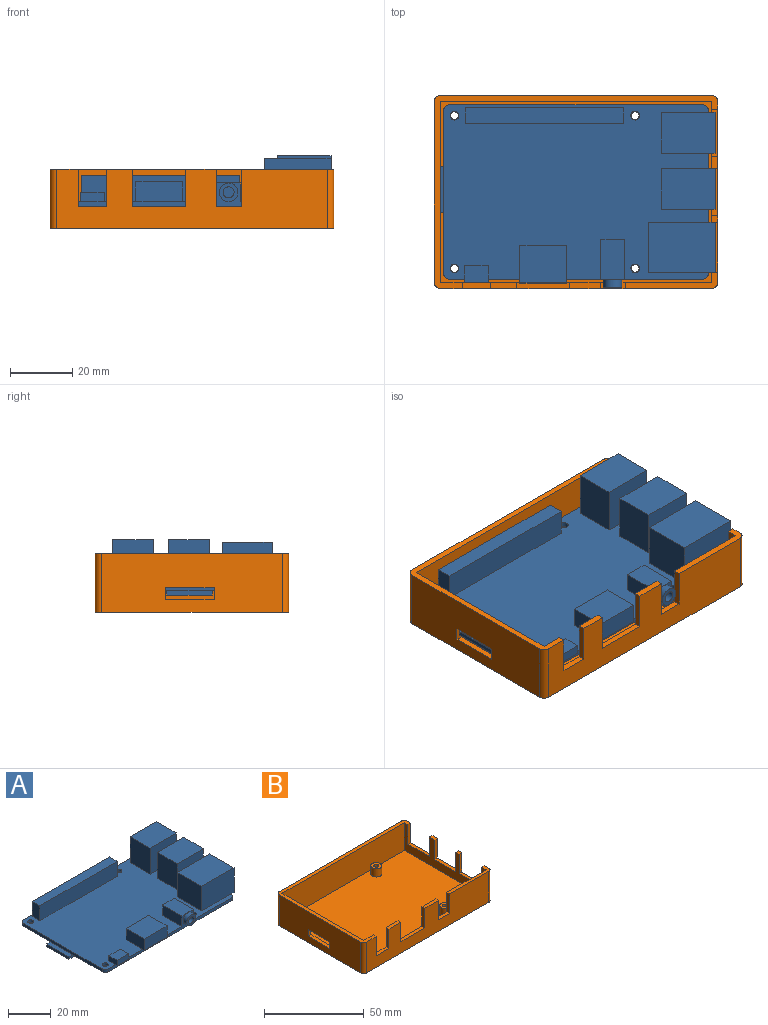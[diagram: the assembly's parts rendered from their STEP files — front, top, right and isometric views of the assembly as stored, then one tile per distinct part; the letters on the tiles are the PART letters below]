
ASSEMBLY  parts=2 mates=1
PART A: 68 faces, bbox 89.5x58.5x18.2 mm
  f0: plane 85x56mm, normal (0,0,1), area 3489.1mm2, adj f1,f2,f3,f4,f5,f6,f7,f8
  f1: plane 81x1.6mm, normal (0,1,0), area 129.6mm2, adj f0,f2,f12,f13
  f2: cylinder r=2mm len=2mm, axis (0,0,-1), area 5mm2, adj f0,f1,f3,f13
  f3: plane 52x1.6mm, normal (-1,0,0), area 83.2mm2, adj f0,f2,f4,f13,f42
  f4: cylinder r=2mm len=2mm, axis (0,0,-1), area 5mm2, adj f0,f3,f5,f13
  f5: plane 81x7.6mm, normal (0,-1,0), area 146.3mm2, adj f0,f4,f6,f13,f48,f54,f60,f62
  f6: cylinder r=2mm len=2mm, axis (0,0,-1), area 5mm2, adj f0,f5,f7,f13
  f7: plane 52x1.6mm, normal (1,0,0), area 83.2mm2, adj f0,f6,f12,f13,f14,f20,f26
  f8: cylinder r=1.4mm len=2.8mm, axis (0,0,-1), area 14.1mm2, adj f0,f13
  f9: cylinder r=1.4mm len=2.8mm, axis (0,0,-1), area 14.1mm2, adj f0,f13
  f10: cylinder r=1.4mm len=2.8mm, axis (0,0,-1), area 14.1mm2, adj f0,f13
  f11: cylinder r=1.4mm len=2.8mm, axis (0,0,-1), area 14.1mm2, adj f0,f13
  f12: cylinder r=2mm len=2mm, axis (0,0,-1), area 5mm2, adj f0,f1,f7,f13
  f13: plane 85x56mm, normal (0,0,-1), area 4264.8mm2, adj f1,f2,f3,f4,f5,f6,f7,f8
  f14: plane 13.1x2.1mm, normal (0,0,-1), area 27.5mm2, adj f7,f15,f16,f17
  f15: plane 17.2x14.8mm, normal (0,-1,0), area 254.6mm2, adj f0,f14,f16,f18,f19
  f16: plane 14.8x13.1mm, normal (1,0,0), area 193.9mm2, adj f14,f15,f17,f19
  f17: plane 17.2x14.8mm, normal (0,1,0), area 254.6mm2, adj f0,f14,f16,f18,f19
  f18: plane 14.8x13.1mm, normal (-1,0,0), area 193.9mm2, adj f0,f15,f17,f19
  f19: plane 17.2x13.1mm, normal (0,0,1), area 225.3mm2, adj f15,f16,f17,f18
  f20: plane 13.1x2.1mm, normal (0,0,-1), area 27.5mm2, adj f7,f21,f22,f23
  f21: plane 17.2x14.8mm, normal (0,-1,0), area 254.6mm2, adj f0,f20,f22,f24,f25
  f22: plane 14.8x13.1mm, normal (1,0,0), area 193.9mm2, adj f20,f21,f23,f25
  f23: plane 17.2x14.8mm, normal (0,1,0), area 254.6mm2, adj f0,f20,f22,f24,f25
  f24: plane 14.8x13.1mm, normal (-1,0,0), area 193.9mm2, adj f0,f21,f23,f25
  f25: plane 17.2x13.1mm, normal (0,0,1), area 225.3mm2, adj f21,f22,f23,f24
  f26: plane 15.9x2.1mm, normal (0,0,-1), area 33.4mm2, adj f7,f27,f28,f29
  f27: plane 21.2x14mm, normal (0,-1,0), area 296.8mm2, adj f0,f26,f28,f30,f31
  f28: plane 15.9x14mm, normal (1,0,0), area 222.6mm2, adj f26,f27,f29,f31
  f29: plane 21.2x14mm, normal (0,1,0), area 296.8mm2, adj f0,f26,f28,f30,f31
  f30: plane 15.9x14mm, normal (-1,0,0), area 222.6mm2, adj f0,f27,f29,f31
  f31: plane 21.2x15.9mm, normal (0,0,1), area 337.1mm2, adj f27,f28,f29,f30
  f32: plane 8.5x5mm, normal (-1,0,0), area 42.5mm2, adj f0,f33,f35,f36
  f33: plane 50.8x8.5mm, normal (0,-1,0), area 431.8mm2, adj f0,f32,f34,f36
  f34: plane 8.5x5mm, normal (1,0,0), area 42.5mm2, adj f0,f33,f35,f36
  f35: plane 50.8x8.5mm, normal (0,1,0), area 431.8mm2, adj f0,f32,f34,f36
  f36: plane 50.8x5mm, normal (0,0,1), area 254mm2, adj f32,f33,f34,f35
  f37: plane 5x1.8mm, normal (-1,0,0), area 9mm2, adj f13,f38,f40,f41
  f38: plane 50.8x1.8mm, normal (0,-1,0), area 91.4mm2, adj f13,f37,f39,f41
  f39: plane 5x1.8mm, normal (1,0,0), area 9mm2, adj f13,f38,f40,f41
  f40: plane 50.8x1.8mm, normal (0,1,0), area 91.4mm2, adj f13,f37,f39,f41
  f41: plane 50.8x5mm, normal (0,0,-1), area 254mm2, adj f37,f38,f39,f40
  f42: plane 14.6x2.4mm, normal (0,0,1), area 35mm2, adj f3,f43,f44,f46
  f43: plane 14.6x1.4mm, normal (-1,0,0), area 20.4mm2, adj f42,f44,f46,f47
  f44: plane 17x1.4mm, normal (0,1,0), area 23.8mm2, adj f13,f42,f43,f45,f47
  f45: plane 14.6x1.4mm, normal (1,0,0), area 20.4mm2, adj f13,f44,f46,f47
  f46: plane 17x1.4mm, normal (0,-1,0), area 23.8mm2, adj f13,f42,f43,f45,f47
  f47: plane 17x14.6mm, normal (0,0,-1), area 248.2mm2, adj f43,f44,f45,f46
  f48: plane 7.5x1mm, normal (0,0,-1), area 7.5mm2, adj f5,f49,f50,f51
  f49: plane 5.4x3mm, normal (-1,0,0), area 16.2mm2, adj f0,f48,f50,f52,f53
  f50: plane 7.5x3mm, normal (0,-1,0), area 22.5mm2, adj f48,f49,f51,f53
  f51: plane 5.4x3mm, normal (1,0,0), area 16.2mm2, adj f0,f48,f50,f52,f53
  f52: plane 7.5x3mm, normal (0,1,0), area 22.5mm2, adj f0,f49,f51,f53
  f53: plane 7.5x5.4mm, normal (0,0,1), area 40.5mm2, adj f49,f50,f51,f52
  f54: plane 15x1.2mm, normal (0,0,-1), area 18mm2, adj f5,f55,f57,f58
  f55: plane 12x6.4mm, normal (1,0,0), area 76.8mm2, adj f0,f54,f56,f58,f59
  f56: plane 15x6.4mm, normal (0,1,0), area 96mm2, adj f0,f55,f57,f59
  f57: plane 12x6.4mm, normal (-1,0,0), area 76.8mm2, adj f0,f54,f56,f58,f59
  f58: plane 15x6.4mm, normal (0,-1,0), area 96mm2, adj f54,f55,f57,f59
  f59: plane 15x12mm, normal (0,0,1), area 180mm2, adj f55,f56,f57,f58
  f60: plane 12.6x6mm, normal (1,0,0), area 75.6mm2, adj f0,f5,f61,f63
  f61: plane 7.5x6mm, normal (0,1,0), area 45mm2, adj f0,f60,f62,f63
  f62: plane 12.6x6mm, normal (-1,0,0), area 75.6mm2, adj f0,f5,f61,f63
  f63: plane 12.6x7.5mm, normal (0,0,1), area 94.5mm2, adj f5,f60,f61,f62
  f64: cylinder r=1.75mm len=3.5mm, axis (0,1,0), area 27.5mm2, adj f66,f67
  f65: cylinder r=3mm len=6mm, axis (0,1,0), area 47.1mm2, adj f5,f66
  f66: plane 6x6mm, normal (0,-1,0), area 18.7mm2, adj f64,f65
  f67: plane 3.5x3.5mm, normal (0,-1,0), area 9.6mm2, adj f64
PART B: 54 faces, bbox 91x62x19 mm
  f0: plane 58x19mm, normal (-1,0,0), area 1039.6mm2, adj f8,f12,f46,f47,f50,f51,f52,f53
  f1: plane 58x17mm, normal (1,0,0), area 923.6mm2, adj f4,f8,f14,f15,f50,f51,f52,f53
  f2: plane 87x19mm, normal (0,-1,0), area 1245mm2, adj f5,f8,f9,f10,f12,f28,f29,f30
  f3: plane 58x19mm, normal (1,0,0), area 548.8mm2, adj f6,f7,f8,f9,f12,f37,f38,f39
  f4: plane 87x17mm, normal (0,1,0), area 1071mm2, adj f1,f5,f8,f9,f10,f13,f15,f28
  f5: plane 8.45x2mm, normal (0,0,1), area 16.9mm2, adj f2,f4,f30,f35
  f6: plane 2.2x2mm, normal (0,0,1), area 4.4mm2, adj f3,f13,f41,f45
  f7: plane 3.9x2mm, normal (0,0,1), area 7.8mm2, adj f3,f13,f38,f42
  f8: plane 91x62mm, normal (0,0,1), area 318.5mm2, adj f0,f1,f2,f3,f4,f11,f13,f14
  f9: plane 29.75x5.3mm, normal (0,0,1), area 65.2mm2, adj f2,f3,f4,f13,f32,f44,f48
  f10: plane 9.75x2mm, normal (0,0,1), area 19.5mm2, adj f2,f4,f29,f33
  f11: plane 87x19mm, normal (0,1,0), area 1653mm2, adj f8,f12,f46,f49
  f12: plane 91x62mm, normal (0,0,-1), area 5618.9mm2, adj f0,f2,f3,f11,f16,f19,f22,f25
  f13: plane 58x17mm, normal (-1,0,0), area 432.8mm2, adj f4,f6,f7,f8,f9,f14,f15,f37
  f14: plane 87x17mm, normal (0,-1,0), area 1479mm2, adj f1,f8,f13,f15
  f15: plane 87x58mm, normal (0,0,1), area 4951mm2, adj f1,f4,f13,f14,f17,f20,f23,f26
  f16: cylinder r=1.25mm len=7mm, axis (0,0,-1), area 55mm2, adj f12,f18
  f17: cylinder r=2.75mm len=5.5mm, axis (0,0,-1), area 86.4mm2, adj f15,f18
  f18: plane 5.5x5.5mm, normal (0,0,1), area 18.8mm2, adj f16,f17
  f19: cylinder r=1.25mm len=7mm, axis (0,0,-1), area 55mm2, adj f12,f21
  f20: cylinder r=2.75mm len=5.5mm, axis (0,0,-1), area 86.4mm2, adj f15,f21
  f21: plane 5.5x5.5mm, normal (0,0,1), area 18.8mm2, adj f19,f20
  f22: cylinder r=1.25mm len=7mm, axis (0,0,-1), area 55mm2, adj f12,f24
  f23: cylinder r=2.75mm len=5.5mm, axis (0,0,-1), area 86.4mm2, adj f15,f24
  f24: plane 5.5x5.5mm, normal (0,0,1), area 18.8mm2, adj f22,f23
  f25: cylinder r=1.25mm len=7mm, axis (0,0,-1), area 55mm2, adj f12,f27
  f26: cylinder r=2.75mm len=5.5mm, axis (0,0,-1), area 86.4mm2, adj f15,f27
  f27: plane 5.5x5.5mm, normal (0,0,1), area 18.8mm2, adj f25,f26
  f28: plane 17x2mm, normal (0,0,1), area 34mm2, adj f2,f4,f29,f30
  f29: plane 12x2mm, normal (-1,0,0), area 24mm2, adj f2,f4,f10,f28
  f30: plane 12x2mm, normal (1,0,0), area 24mm2, adj f2,f4,f5,f28
  f31: plane 8x2mm, normal (0,0,1), area 16mm2, adj f2,f4,f32,f33
  f32: plane 12x2mm, normal (-1,0,0), area 24mm2, adj f2,f4,f9,f31
  f33: plane 12x2mm, normal (1,0,0), area 24mm2, adj f2,f4,f10,f31
  f34: plane 9x2mm, normal (0,0,1), area 18mm2, adj f2,f4,f35,f36
  f35: plane 12x2mm, normal (-1,0,0), area 24mm2, adj f2,f4,f5,f34
  f36: plane 12x2mm, normal (1,0,0), area 24mm2, adj f2,f4,f8,f34
  f37: plane 15.1x2mm, normal (0,0,1), area 30.2mm2, adj f3,f13,f38,f39
  f38: plane 12x2mm, normal (0,1,0), area 24mm2, adj f3,f7,f13,f37
  f39: plane 12x2mm, normal (0,-1,0), area 24mm2, adj f3,f8,f13,f37
  f40: plane 15.1x2mm, normal (0,0,1), area 30.2mm2, adj f3,f13,f41,f42
  f41: plane 12x2mm, normal (0,1,0), area 24mm2, adj f3,f6,f13,f40
  f42: plane 12x2mm, normal (0,-1,0), area 24mm2, adj f3,f7,f13,f40
  f43: plane 15.9x2mm, normal (0,0,1), area 31.8mm2, adj f3,f13,f44,f45
  f44: plane 12x2mm, normal (0,1,0), area 24mm2, adj f3,f9,f13,f43
  f45: plane 12x2mm, normal (0,-1,0), area 24mm2, adj f3,f6,f13,f43
  f46: cylinder r=2mm len=19mm, axis (0,0,-1), area 59.7mm2, adj f0,f8,f11,f12
  f47: cylinder r=2mm len=19mm, axis (0,0,1), area 59.7mm2, adj f0,f2,f8,f12
  f48: cylinder r=2mm len=19mm, axis (0,0,-1), area 59.7mm2, adj f2,f3,f9,f12
  f49: cylinder r=2mm len=19mm, axis (0,0,1), area 59.7mm2, adj f3,f8,f11,f12
  f50: plane 4x2mm, normal (0,-1,0), area 8mm2, adj f0,f1,f52,f53
  f51: plane 4x2mm, normal (0,1,0), area 8mm2, adj f0,f1,f52,f53
  f52: plane 15.6x2mm, normal (0,0,1), area 31.2mm2, adj f0,f1,f50,f51
  f53: plane 15.6x2mm, normal (0,0,-1), area 31.2mm2, adj f0,f1,f50,f51
PLACE A t=(0.55,21.84,16.08)mm
PLACE B t=(-2.45,18.84,9.08)mm fixed
MATE fastened A.f8 <-> B.f16  axis (0,0,-1) through (4.05,74.34,16.08)mm
